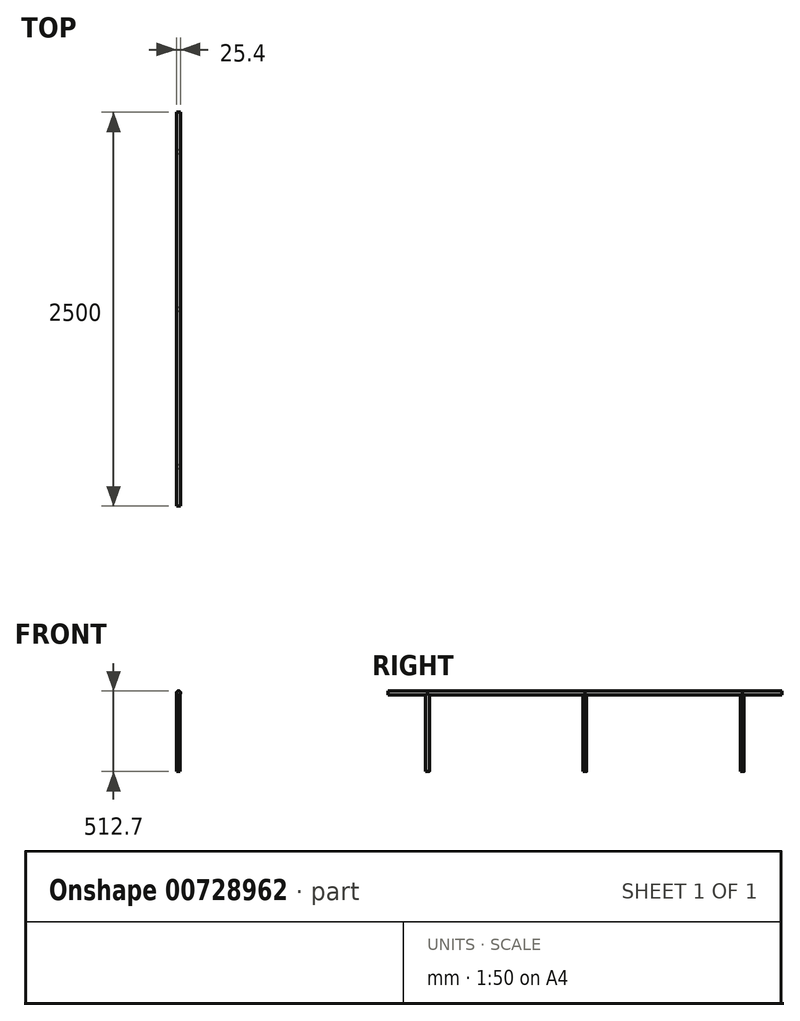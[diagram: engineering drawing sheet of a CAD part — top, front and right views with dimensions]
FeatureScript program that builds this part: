
annotation { "Feature Type Name" : "Feature", "Feature Type Description" : "" }
export const myFeature = defineFeature(function(context is Context, id is Id, definition is map)
    precondition{}
    {
        {
            var Q0;
            Q0=qCreatedBy(makeId("Front.planeOp"),FACE);
            var sketch = newSketch(context, id + "F0", { "sketchPlane" : qUnion([Q0])});
            skCircle(sketch, "E0", {"center": v(0, 0) * mm, "radius": 12.7 * mm});
            skSolve(sketch);
        }
        {
            var Q0;
            Q0 = qSketchRegion(id + "F0", true);
            extrude(context, id + "F1", {"entities" : qUnion([Q0]), "endBound" : BoundingType.SYMMETRIC, "depth" : 2500 * mm, "offsetDistance" : 25 * mm});
        }
        {
            var Q0;
            Q0=qCreatedBy(makeId("Top.planeOp"),FACE);
            var sketch = newSketch(context, id + "F2", { "sketchPlane" : qUnion([Q0])});
            skCircle(sketch, "E1", {"center": v(0, 0) * mm, "radius": 11.2 * mm});
            skCircle(sketch, "E2", {"center": v(0, -1000) * mm, "radius": 11.2 * mm});
            skCircle(sketch, "E3", {"center": v(0, 1000) * mm, "radius": 11.2 * mm});
            skSolve(sketch);
        }
        {
            var Q0;
            Q0 = qSketchRegion(id + "F2", true);
            extrude(context, id + "F3", {"entities" : qUnion([Q0]), "operationType" : NewBodyOperationType.ADD, "oppositeDirection" : true, "depth" : 500 * mm, "offsetDistance" : 25 * mm});
        }
    });
